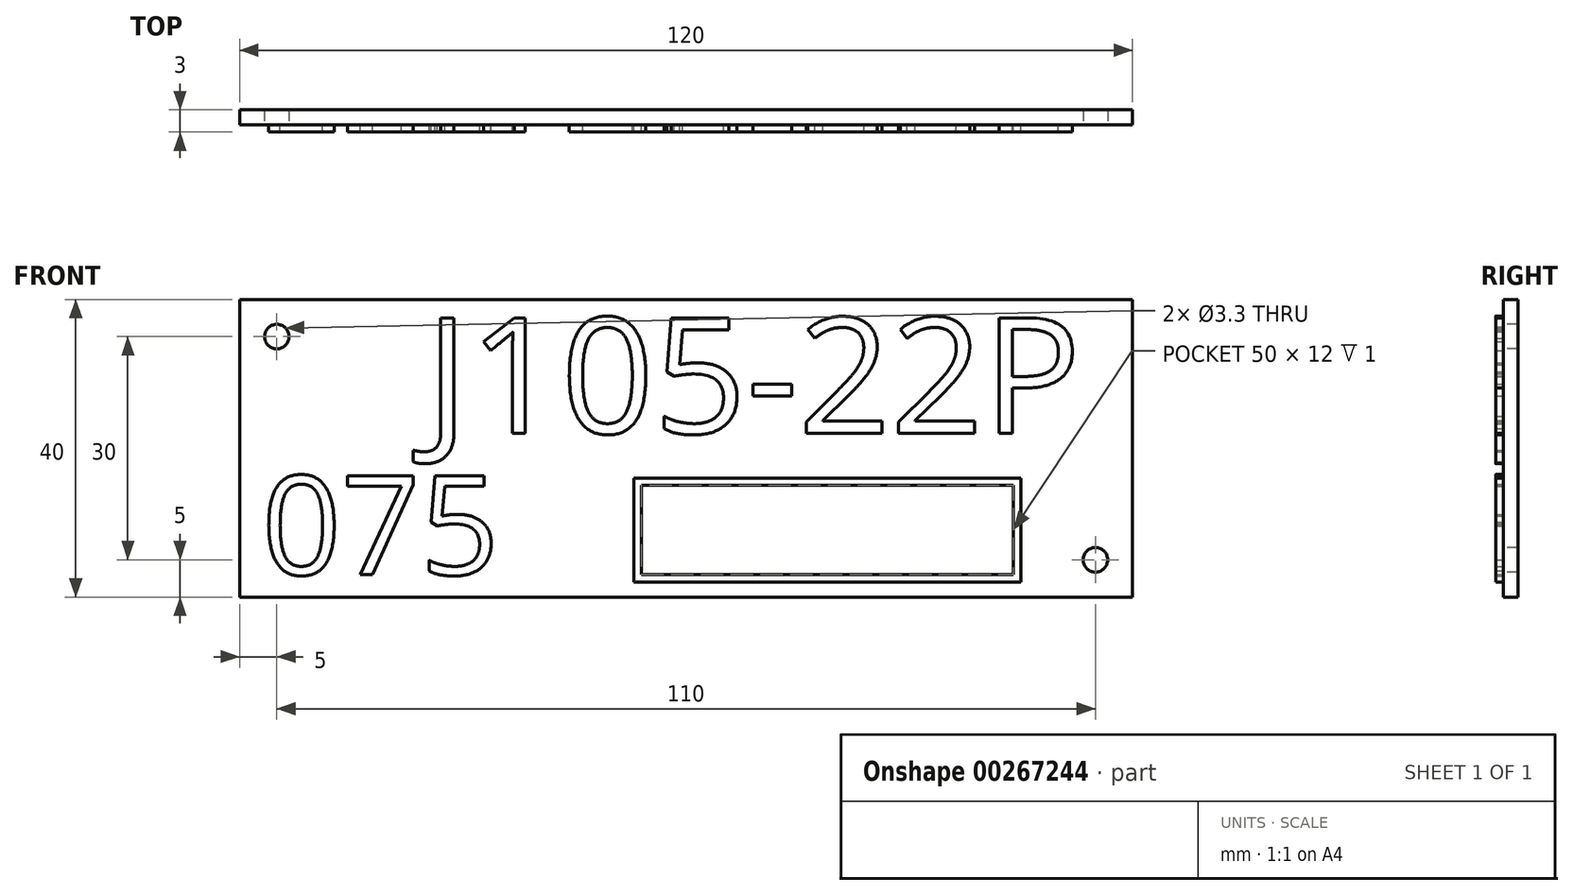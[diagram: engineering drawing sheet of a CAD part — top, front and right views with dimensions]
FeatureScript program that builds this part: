
annotation { "Feature Type Name" : "Feature", "Feature Type Description" : "" }
export const myFeature = defineFeature(function(context is Context, id is Id, definition is map)
    precondition{}
    {
        {
            var Q0;
            Q0=qCreatedBy(makeId("Front.planeOp"),FACE);
            var sketch = newSketch(context, id + "F0", { "sketchPlane" : qUnion([Q0])});
            skLineSegment(sketch, "E0.bottom", {"start": v(60, -20) * mm, "end": v(-60, -20) * mm});
            skLineSegment(sketch, "E0.top", {"start": v(60, 20) * mm, "end": v(-60, 20) * mm});
            skLineSegment(sketch, "E0.left", {"start": v(60, -20) * mm, "end": v(60, 20) * mm});
            skLineSegment(sketch, "E0.right", {"start": v(-60, -20) * mm, "end": v(-60, 20) * mm});
            skPoint(sketch, "E0.middle", {"position": v(0, 0) * mm});
            skSolve(sketch);
        }
        {
            var Q0;
            Q0=makeQuery(id+"F0.imprint","IMPRINT",FACE,{"disambiguationData":[TD([[makeQuery(id+"F0.imprint","IMPRINT",EDGE,{"derivedFrom":sQuery(id+"F0.wireOp",EDGE,"E0.bottom")}),-1.0]])]});
            extrude(context, id + "F1", {"entities" : qUnion([Q0]), "depth" : 2 * mm});
        }
        {
            var Q0;
            Q0=makeQuery(id+"F1.opExtrude","CAP_FACE",FACE,{"disambiguationData":[OSD([sQuery(id+"F0.wireOp",EDGE,"E0.bottom"),sQuery(id+"F0.wireOp",EDGE,"E0.top"),sQuery(id+"F0.wireOp",EDGE,"E0.left"),sQuery(id+"F0.wireOp",EDGE,"E0.right")])],"isStart":false});
            var sketch = newSketch(context, id + "F2", { "sketchPlane" : qUnion([Q0])});
            skPoint(sketch, "E1", {"position": v(-55, 15) * mm});
            skPoint(sketch, "E2", {"position": v(55, -15) * mm});
            skSolve(sketch);
        }
        {
            var Q0;
            Q0=sQuery(id+"F2.wireOp",VERTEX,"E1");
            var Q1;
            Q1=sQuery(id+"F2.wireOp",VERTEX,"E2");
            var Q2;
            Q2=makeQuery(id+"F1.opExtrude","SWEPT_BODY",BODY,{"disambiguationData":[OSD([sQuery(id+"F0.wireOp",EDGE,"E0.bottom"),sQuery(id+"F0.wireOp",EDGE,"E0.top"),sQuery(id+"F0.wireOp",EDGE,"E0.left"),sQuery(id+"F0.wireOp",EDGE,"E0.right")])]});
            hole(context, id + "F3", {"style" : HoleStyle.SIMPLE, "endStyle" : HoleEndStyle.THROUGH, "holeDiameter" : 3.3 * mm, "locations" : qUnion([Q0, Q1]), "scope" : qUnion([Q2]), "isTappedThrough" : true});
        }
        {
            var Q0;
            Q0=makeQuery(id+"F1.opExtrude","CAP_FACE",FACE,{"disambiguationData":[OSD([sQuery(id+"F0.wireOp",EDGE,"E0.bottom"),sQuery(id+"F0.wireOp",EDGE,"E0.top"),sQuery(id+"F0.wireOp",EDGE,"E0.left"),sQuery(id+"F0.wireOp",EDGE,"E0.right")])],"isStart":false});
            var sketch = newSketch(context, id + "F4", { "sketchPlane" : qUnion([Q0])});
            skText(sketch, "E3", { "text": "J105-22P", "fontName": "OpenSans-Regular.ttf"});
            const initialGuessF4  = {"E3": [-0.035, 0.002, 1, 0, 0.01565]};
            skSetInitialGuess(sketch, initialGuessF4);
            skSolve(sketch);
        }
        {
            var Q0;
            Q0=qSketchRegion(id+"F4",true);
            extrude(context, id + "F5", {"entities" : qUnion([Q0]), "operationType" : NewBodyOperationType.ADD, "depth" : 1 * mm});
        }
        {
            var Q0;
            {var subQ0=sQuery(id+"F0.wireOp",EDGE,"E0.top");var subQ1=sQuery(id+"F0.wireOp",EDGE,"E0.left");var subQ2=sQuery(id+"F0.wireOp",EDGE,"E0.right");var subQ3=sQuery(id+"F0.wireOp",EDGE,"E0.bottom");Q0=makeQuery(id+"F5.boolean.opBoolean","SPLIT",FACE,{"disambiguationData":[TD([makeQuery(id+"F1.opExtrude","SWEPT_FACE",FACE,{"disambiguationData":[OSD([subQ3])]})])],"derivedFrom":makeQuery(id+"F1.opExtrude","CAP_FACE",FACE,{"disambiguationData":[OSD([subQ3,subQ0,subQ1,subQ2])],"isStart":false})});}
            var sketch = newSketch(context, id + "F6", { "sketchPlane" : qUnion([Q0])});
            skText(sketch, "E4", { "text": "075", "fontName": "OpenSans-Regular.ttf"});
            const initialGuessF6  = {"E4": [-0.057, -0.017, 1, 0, 0.01338]};
            skSetInitialGuess(sketch, initialGuessF6);
            skSolve(sketch);
        }
        {
            var Q0;
            Q0=qSketchRegion(id+"F6",true);
            extrude(context, id + "F7", {"entities" : qUnion([Q0]), "operationType" : NewBodyOperationType.ADD, "depth" : 1 * mm});
        }
        {
            var Q0;
            {var subQ46=sQuery(id+"F0.wireOp",EDGE,"E0.top");var subQ48=sQuery(id+"F0.wireOp",EDGE,"E0.left");var subQ66=sQuery(id+"F0.wireOp",EDGE,"E0.right");var subQ76=sQuery(id+"F0.wireOp",EDGE,"E0.bottom");var subQ77=makeQuery(id+"F1.opExtrude","SWEPT_FACE",FACE,{"disambiguationData":[OSD([subQ76])]});Q0=makeQuery(id+"F7.boolean.opBoolean","SPLIT",FACE,{"disambiguationData":[TD([subQ77])],"derivedFrom":makeQuery(id+"F5.boolean.opBoolean","SPLIT",FACE,{"disambiguationData":[TD([subQ77])],"derivedFrom":makeQuery(id+"F1.opExtrude","CAP_FACE",FACE,{"disambiguationData":[OSD([subQ76,subQ46,subQ48,subQ66])],"isStart":false})})});}
            var sketch = newSketch(context, id + "F8", { "sketchPlane" : qUnion([Q0])});
            skLineSegment(sketch, "E5.bottom", {"start": v(45, -18) * mm, "end": v(-7, -18) * mm});
            skLineSegment(sketch, "E5.top", {"start": v(45, -4) * mm, "end": v(-7, -4) * mm});
            skLineSegment(sketch, "E5.left", {"start": v(45, -18) * mm, "end": v(45, -4) * mm});
            skLineSegment(sketch, "E5.right", {"start": v(-7, -18) * mm, "end": v(-7, -4) * mm});
            skPoint(sketch, "E5.middle", {"position": v(19, -11) * mm});
            skLineSegment(sketch, "E6.0", {"start": v(44, -5) * mm, "end": v(-6, -5) * mm});
            skLineSegment(sketch, "E6.1", {"start": v(44, -17) * mm, "end": v(44, -5) * mm});
            skLineSegment(sketch, "E6.2", {"start": v(44, -17) * mm, "end": v(-6, -17) * mm});
            skLineSegment(sketch, "E6.3", {"start": v(-6, -17) * mm, "end": v(-6, -5) * mm});
            skSolve(sketch);
        }
        {
            var Q0;
            Q0=makeQuery(id+"F8.imprint","IMPRINT",FACE,{"disambiguationData":[TD([[makeQuery(id+"F8.imprint","IMPRINT",EDGE,{"derivedFrom":sQuery(id+"F8.wireOp",EDGE,"E5.bottom")}),-1.0]])]});
            extrude(context, id + "F9", {"entities" : qUnion([Q0]), "operationType" : NewBodyOperationType.ADD, "depth" : 1 * mm});
        }
    });
